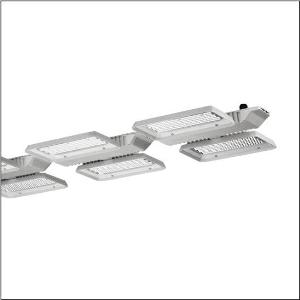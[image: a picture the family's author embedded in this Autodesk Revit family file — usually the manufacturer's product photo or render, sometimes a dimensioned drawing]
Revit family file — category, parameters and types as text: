
# Revit family: highbay_11_51hla1d34sca
name_source: partatom
category: Lighting Fixtures
units: mm (PartAtom-declared; Revit-internal decimal feet)

## family parameters
Cut with Voids When Loaded = No
Host = Face
Light Source = No
Part Type = Normal
Room Calculation Point = No
Round Connector Dimension = Use Diameter
Shared = No

## types (1)
- --- (1 x LED, 48560 lm, 284.4 W, 4000K)
    Apparent Load = 284 VA
    CIE Flux Codes = 88 95 99 100 99
    Color Rendering = 80
    Color Temperature = 4000K
    Default Elevation = 1800 mm
    Description = Highbay 11, LED high bay luminaire, primary light control with lens, of PMMA, light emission: direct distribution, primary light characteristic: symmetric, installation type: suspended mounting, for 3x 2x LED, rated luminous flux: 48.560lm, luminous efficacy: 171lm/W, light colour: 840, colour temperature: 4000K, control gear: ECG DALI, with terminal, 5-pole, max. 2.5mm², mains connection: 230..240V, AC, 50/60Hz, rated input power: 284W, LED unit, of diecast aluminium, unplated, bead blasted, silver, length: 1.410mm, width: 500mm, height: 65mm, housing, of diecast aluminium, uncoated, bead blasted, silver, protection rating (complete): IP65, insulation class (complete): insulation class I (protective earthing), certification: CE, ENEC, VDE, UKCA, protection symbol: D, impact resistance: IK08 with glass or PC cover, permissible operating ambient temperature: -35..+45°C, reducing of maximum allowable ambient temperature of 5°C with ceiling mounting, corresponds to IFS (International Featured Standards) requirements for safety and quality in the food industry, packaging unit: 1 piece
    Height = 95 mm
    Lamp = 1 x LED
    Lamp Light Flux = 48560 lm
    Lamp Power = 284.4 W
    Lamp count = 1
    Length = 1410 mm
    Luminous efficacy = 171 lm/W
    Manufacturer = Siteco
    ModVariant = No
    Model = 51HLA1D34SCA
    Mounting Place = Ceiling
    Mounting Type = Pendant
    Number of Poles = 1
    OnlyDefault = Yes
    Power Factor = 1
    Product Name = Highbay 11
    Product group = LED high bay luminaire
    ProductGroupID = 903
    Protection Class = Protection class I
    Protection Degree = IP 65
    RLX_Detail_Level = 1
    RLX_Emergency_Light_Flux = 0 lm
    RLX_Emergency_Type = 0
    RLX_Emergency_Type_DB = No
    RlxData = <blob elided: 105385 chars, md5=8cbb25c6>
    Socket = socket
    Standby Power = 0 W
    System Light Flux = 48560 lm
    System Power = 284 W
    Type Comments = factory setting: luminous flux: 100 % | dim-lin: 254 | 535 mA
    Type Image = l_1003314.jpg
    URL = http://relux.com
    VarID = @adj_160217
    Voltage = 0 V
    Weight = 0.00 kg
    Width = 501 mm

## geometry (parser evidence)
native form markers: Blend x4, Sweep x10
no freeform markers — native parametric forms only
